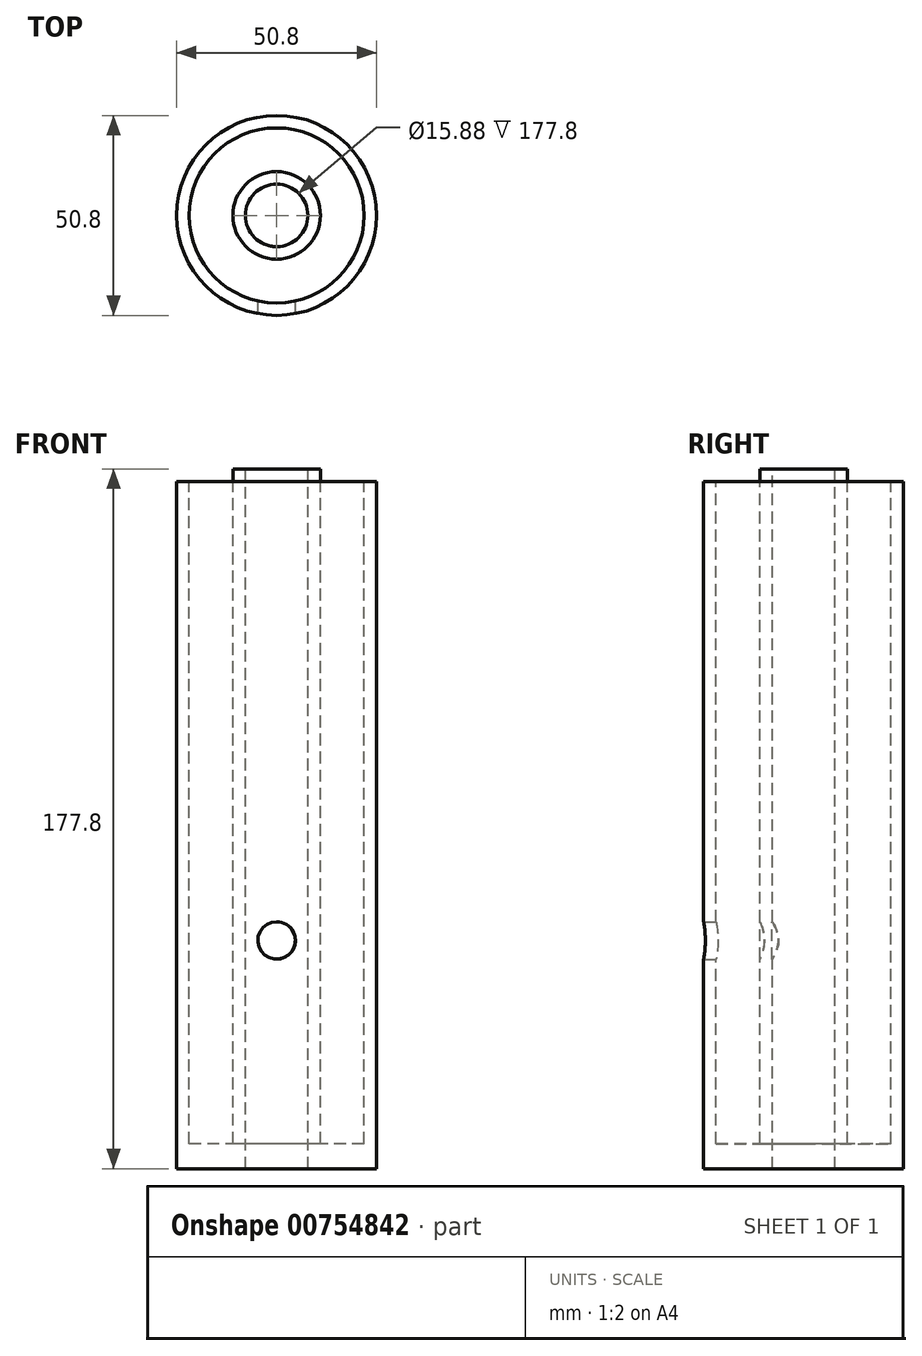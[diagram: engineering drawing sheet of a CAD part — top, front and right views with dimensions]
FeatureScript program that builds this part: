
annotation { "Feature Type Name" : "Feature", "Feature Type Description" : "" }
export const myFeature = defineFeature(function(context is Context, id is Id, definition is map)
    precondition{}
    {
        {
            var Q0;
            Q0=qCreatedBy(makeId("Top.planeOp"),FACE);
            var sketch = newSketch(context, id + "F0", { "sketchPlane" : qUnion([Q0])});
            skCircle(sketch, "E0", {"center": v(0, 0) * mm, "radius": 25.4 * mm});
            skSolve(sketch);
        }
        {
            var Q0;
            Q0 = qSketchRegion(id + "F0", true);
            extrude(context, id + "F1", {"entities" : qUnion([Q0]), "depth" : 177.8 * mm, "offsetDistance" : 25.4 * mm});
        }
        {
            var Q0;
            Q0=makeQuery(id+"F1.opExtrude","CAP_FACE",FACE,{"disambiguationData":[OSD([sQuery(id+"F0.wireOp",EDGE,"E0")])],"isStart":false});
            var sketch = newSketch(context, id + "F2", { "sketchPlane" : qUnion([Q0])});
            skCircle(sketch, "E1", {"center": v(0, 0) * mm, "radius": 7.94 * mm});
            skSolve(sketch);
        }
        {
            var Q0;
            Q0 = qSketchRegion(id + "F2", true);
            extrude(context, id + "F3", {"entities" : qUnion([Q0]), "operationType" : NewBodyOperationType.REMOVE, "oppositeDirection" : true, "depth" : 240.8 * mm, "offsetDistance" : 25.4 * mm});
        }
        {
            var Q0;
            Q0=makeQuery(id+"F1.opExtrude","CAP_FACE",FACE,{"disambiguationData":[OSD([sQuery(id+"F0.wireOp",EDGE,"E0")])],"isStart":false});
            var sketch = newSketch(context, id + "F4", { "sketchPlane" : qUnion([Q0])});
            skCircle(sketch, "E2", {"center": v(0, 0) * mm, "radius": 22.23 * mm});
            skCircle(sketch, "E3", {"center": v(0, 0) * mm, "radius": 11.11 * mm});
            skSolve(sketch);
        }
        {
            var Q0;
            Q0 = qSketchRegion(id + "F4", true);
            extrude(context, id + "F5", {"entities" : qUnion([Q0]), "operationType" : NewBodyOperationType.REMOVE, "oppositeDirection" : true, "depth" : 171.45 * mm, "offsetDistance" : 25.4 * mm});
        }
        {
            var Q0;
            {var subQ0=sQuery(id+"F0.wireOp",EDGE,"E0");Q0=makeQuery(id+"F5.boolean.opBoolean","SPLIT",FACE,{"disambiguationData":[TD([makeQuery(id+"F1.opExtrude","SWEPT_FACE",FACE,{"disambiguationData":[OSD([subQ0])]})])],"derivedFrom":makeQuery(id+"F1.opExtrude","CAP_FACE",FACE,{"disambiguationData":[OSD([subQ0])],"isStart":false})});}
            var sketch = newSketch(context, id + "F6", { "sketchPlane" : qUnion([Q0])});
            skCircle(sketch, "E4", {"center": v(0, 0) * mm, "radius": 28.6 * mm});
            skCircle(sketch, "E5", {"center": v(0, 0) * mm, "radius": 14.62 * mm});
            skSolve(sketch);
        }
        {
            var Q0;
            Q0 = qSketchRegion(id + "F6", true);
            extrude(context, id + "F7", {"entities" : qUnion([Q0]), "operationType" : NewBodyOperationType.REMOVE, "oppositeDirection" : true, "depth" : 3.17 * mm, "offsetDistance" : 25.4 * mm});
        }
        {
            var Q0;
            Q0=qCreatedBy(makeId("Front.planeOp"),FACE);
            var sketch = newSketch(context, id + "F8", { "sketchPlane" : qUnion([Q0])});
            skCircle(sketch, "E6", {"center": v(0, 57.98) * mm, "radius": 4.76 * mm});
            skSolve(sketch);
        }
        {
            var Q0;
            Q0 = qSketchRegion(id + "F8", true);
            extrude(context, id + "F9", {"entities" : qUnion([Q0]), "operationType" : NewBodyOperationType.REMOVE, "depth" : 34.54 * mm, "offsetDistance" : 25.4 * mm});
        }
        {
            var Q0;
            Q0=makeQuery(id+"F5.boolean.opBoolean","SPLIT",FACE,{"disambiguationData":[TD([makeQuery(id+"F3.boolean.opBoolean","COPY",FACE,{"derivedFrom":makeQuery(id+"F3.opExtrude","SWEPT_FACE",FACE,{"disambiguationData":[OSD([sQuery(id+"F2.wireOp",EDGE,"E1")])]})})])],"derivedFrom":makeQuery(id+"F1.opExtrude","CAP_FACE",FACE,{"disambiguationData":[OSD([sQuery(id+"F0.wireOp",EDGE,"E0")])],"isStart":false})});
            var sketch = newSketch(context, id + "F10", { "sketchPlane" : qUnion([Q0])});
            skCircle(sketch, "E7", {"center": v(0, 0) * mm, "radius": 11.06 * mm});
            skCircle(sketch, "E8", {"center": v(0, 0) * mm, "radius": 8.08 * mm});
            skSolve(sketch);
        }
        {
            var Q0;
            Q0 = qSketchRegion(id + "F10", true);
            extrude(context, id + "F11", {"entities" : qUnion([Q0]), "operationType" : NewBodyOperationType.ADD, "oppositeDirection" : true, "depth" : 130.56 * mm, "offsetDistance" : 25.4 * mm});
        }
    });
